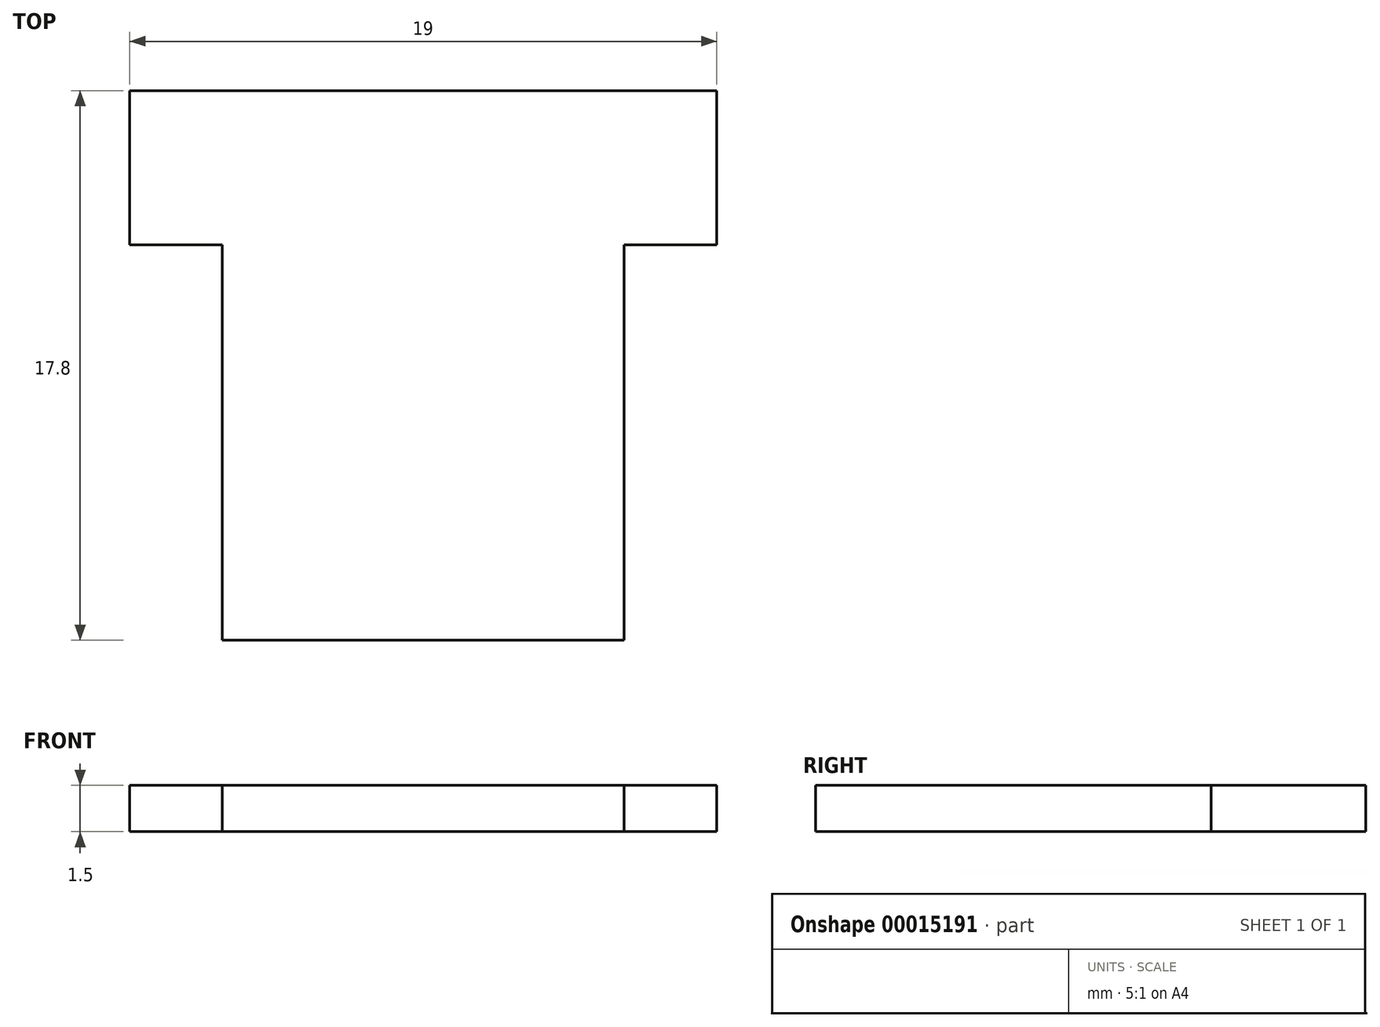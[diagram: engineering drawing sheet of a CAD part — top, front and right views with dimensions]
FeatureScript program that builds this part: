
annotation { "Feature Type Name" : "Feature", "Feature Type Description" : "" }
export const myFeature = defineFeature(function(context is Context, id is Id, definition is map)
    precondition{}
    {
        {
            var Q0;
            Q0=qCreatedBy(makeId("Top.planeOp"),FACE);
            var sketch = newSketch(context, id + "F0", { "sketchPlane" : qUnion([Q0])});
            skLineSegment(sketch, "E0", {"start": v(0, 0) * mm, "end": v(0, 5) * mm});
            skLineSegment(sketch, "E1", {"start": v(0, 5) * mm, "end": v(19, 5) * mm});
            skLineSegment(sketch, "E2", {"start": v(19, 5) * mm, "end": v(19, 0) * mm});
            skLineSegment(sketch, "E3", {"start": v(19, 0) * mm, "end": v(16, 0) * mm});
            skLineSegment(sketch, "E4", {"start": v(16, 0) * mm, "end": v(16, -12.8) * mm});
            skLineSegment(sketch, "E5", {"start": v(16, -12.8) * mm, "end": v(3, -12.8) * mm});
            skLineSegment(sketch, "E6", {"start": v(3, -12.8) * mm, "end": v(3, 0) * mm});
            skLineSegment(sketch, "E7", {"start": v(3, 0) * mm, "end": v(0, 0) * mm});
            skSolve(sketch);
        }
        {
            var Q0;
            Q0=makeQuery(id+"F0.imprint","IMPRINT",FACE,{"disambiguationData":[TD([[makeQuery(id+"F0.imprint","IMPRINT",EDGE,{"derivedFrom":sQuery(id+"F0.wireOp",EDGE,"E0")}),-1.0]])]});
            extrude(context, id + "F1", {"entities" : qUnion([Q0]), "depth" : 1.5 * mm});
        }
    });
